# Revit family: Sanitary_Accessories_Johnson-Suisse_Cube_Soap_Wire_Rack_15x11x5cm
name_source: partatom
category: Plumbing Fixtures
revit_build: Autodesk Revit 2015 (Build: 20140606_1530(x64)
units: mm (PartAtom-declared; Revit-internal decimal feet)

## types (1)
- Cube Soap Wire Rack 15x11x5cm
    BIMobject category = Accessories
    Brand url = http://www.johnsonsuisse.com.au
    Design country = Spain
    EAN code = https://9325304004495
    Edition number = 1
    IFC Classification = Furnishing Element
    Manufacturer country = China
    Manufacturer name = Johnson Suisse
    Material main = Metal
    Material secondary = Chrome
    NBS Reference Code = 35-75-82
    NBS Reference Description = Soap Dishes
    Nominal height = 110 mm  [stored 0.360892 ft]
    Nominal width = 150 mm  [stored 0.492126 ft]
    OmniClass Code = 23-31 25 29 11
    OmniClass Description = Hand Soap Holders
    Product Guid = 975e30a4-bdfa-4e18-b95d-4d2cbdd4439e
    Product SKU = GDC160149
    Product data url = https://bimobject.com
    Product family = Cube
    Product group = Accessories
    Product url = https://johnsonsuisse.com.au
    QR code = http://bimobject.com
    Technical description = https://johnsonsuisse.com.au
    Type = cube_soap_wire_rack_15x11x5cm : Default
    UNSPSC Code = 301815
    Uniclass 1.4 Code = L8246
    Uniclass 1.4 Description = Soap holders/dispensers
    Uniclass 2.0 Code = PR-35-75-82
    Uniclass 2.0 Description = Soap Dishes
    Uniclass 2015 Code = Pr_40_20_76_82
    Uniclass 2015 Name = Soap dishes
    Weight Net (Kg) = 0.35

note: [stored X ft] marks values corroborated as IEEE doubles in the binary element streams (Revit-internal decimal feet)

## geometry (parser evidence)
native form markers: Sweep x5
no freeform markers — native parametric forms only
